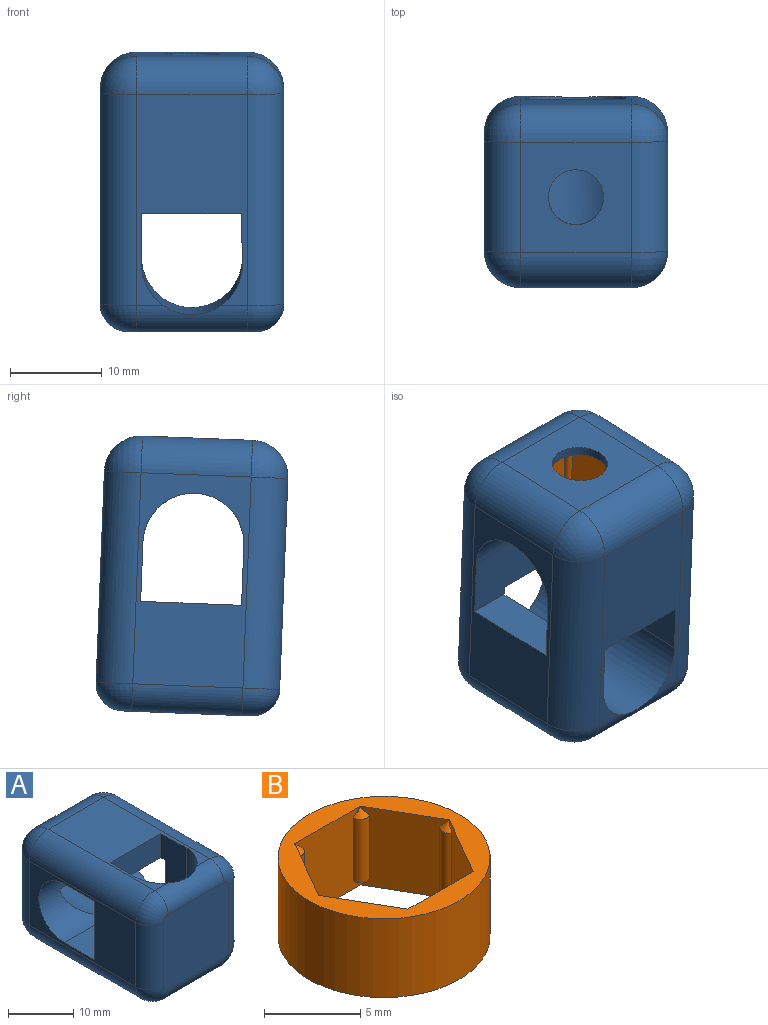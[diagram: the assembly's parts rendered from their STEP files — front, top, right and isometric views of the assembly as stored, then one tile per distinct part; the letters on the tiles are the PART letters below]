
ASSEMBLY  parts=2 mates=1
PART A: 40 faces, bbox 20x30x20 mm
  f0: cylinder r=5.5mm len=11mm, axis (-1,0,0), area 112.3mm2, adj f3,f13,f15,f18
  f1: plane 20x5.5mm, normal (1,0,0), area 99mm2, adj f2,f6,f7,f10,f11,f13,f15,f16
  f2: plane 10.87x4.5mm, normal (0,-1,0), area 48.9mm2, adj f1,f5,f10,f13
  f3: plane 23x12mm, normal (1,0,0), area 157mm2, adj f0,f12,f13,f15,f25,f28,f31,f32
  f4: plane 23x12mm, normal (-1,0,0), area 157mm2, adj f13,f14,f15,f16,f20,f21,f22,f39
  f5: plane 20x5.36mm, normal (-1,-0.02,0), area 96.3mm2, adj f2,f6,f7,f10,f11,f12,f13,f15
  f6: cylinder r=5.5mm len=20mm, axis (0,0,-1), area 347.1mm2, adj f1,f5,f10,f11,f35,f36
  f7: plane 10.87x4.5mm, normal (0,-1,0), area 48.9mm2, adj f1,f5,f11,f15
  f8: plane 12x12mm, normal (0,1,0), area 115.7mm2, adj f17,f21,f26,f27,f31
  f9: plane 14x14mm, normal (0,-1,0), area 195.1mm2, adj f32,f33,f34,f35,f36,f37,f38,f39
  f10: plane 23x12mm, normal (0,0,1), area 172.6mm2, adj f1,f2,f5,f6,f20,f25,f26,f35
  f11: plane 23x12mm, normal (0,0,-1), area 172.6mm2, adj f1,f5,f6,f7,f22,f27,f28,f36
  f12: plane 11x4.61mm, normal (0,1,0), area 50.7mm2, adj f3,f5,f13,f15
  f13: plane 20x6.5mm, normal (0,0,-1), area 119.1mm2, adj f0,f1,f2,f3,f4,f5,f12,f14
  f14: cylinder r=5.5mm len=11mm, axis (-1,0,0), area 112.3mm2, adj f4,f13,f15,f18
  f15: plane 20x6.5mm, normal (0,0,1), area 119.1mm2, adj f0,f1,f3,f4,f5,f7,f12,f14
  f16: plane 11x4.5mm, normal (0,1,0), area 49.5mm2, adj f1,f4,f13,f15
  f17: cylinder r=3mm len=6mm, axis (0,1,0), area 18.8mm2, adj f8,f19
  f18: cylinder r=5.5mm len=11mm, axis (0,1,0), area 241.9mm2, adj f0,f14,f19
  f19: plane 11x11mm, normal (0,-1,0), area 66.8mm2, adj f17,f18
  f20: cylinder r=4mm len=23mm, axis (0,1,0), area 144.5mm2, adj f4,f10,f23,f37
  f21: cylinder r=4mm len=12mm, axis (0,0,-1), area 75.4mm2, adj f4,f8,f23,f24
  f22: cylinder r=4mm len=23mm, axis (0,-1,0), area 144.5mm2, adj f4,f11,f24,f38
  f23: sphere r=4mm, area 25.1mm2, adj f20,f21,f26
  f24: sphere r=4mm, area 25.1mm2, adj f21,f22,f27
  f25: cylinder r=4mm len=23mm, axis (0,-1,0), area 144.5mm2, adj f3,f10,f29,f33
  f26: cylinder r=4mm len=12mm, axis (1,0,0), area 75.4mm2, adj f8,f10,f23,f29
  f27: cylinder r=4mm len=12mm, axis (-1,0,0), area 75.4mm2, adj f8,f11,f24,f30
  f28: cylinder r=4mm len=23mm, axis (0,1,0), area 144.5mm2, adj f3,f11,f30,f34
  f29: sphere r=4mm, area 25.1mm2, adj f25,f26,f31
  f30: sphere r=4mm, area 25.1mm2, adj f27,f28,f31
  f31: cylinder r=4mm len=12mm, axis (0,0,1), area 75.4mm2, adj f3,f8,f29,f30
  f32: cylinder r=3mm len=12mm, axis (0,0,-1), area 56.5mm2, adj f3,f9,f33,f34
  f33: torus R=1mm, axis (0,-1,0), area 21.5mm2, adj f9,f25,f32,f35
  f34: torus R=1mm, axis (0,-1,0), area 21.5mm2, adj f9,f28,f32,f36
  f35: cylinder r=3mm len=12mm, axis (-1,0,0), area 52.2mm2, adj f6,f9,f10,f33,f37
  f36: cylinder r=3mm len=12mm, axis (1,0,0), area 52.2mm2, adj f6,f9,f11,f34,f38
  f37: torus R=1mm, axis (0,-1,0), area 21.5mm2, adj f9,f20,f35,f39
  f38: torus R=1mm, axis (0,-1,0), area 21.5mm2, adj f9,f22,f36,f39
  f39: cylinder r=3mm len=12mm, axis (0,0,1), area 56.5mm2, adj f4,f9,f37,f38
PART B: 27 faces, bbox 11x11x5 mm
  f0: plane 5x4.15mm, normal (0.87,-0.5,0), area 19.5mm2, adj f7,f8,f21,f22,f23,f24,f25,f26
  f1: plane 5x4.79mm, normal (0,-1,0), area 19.5mm2, adj f7,f8,f9,f10,f11,f21,f22,f23
  f2: plane 5x4.15mm, normal (-0.87,-0.5,0), area 19.5mm2, adj f7,f8,f9,f10,f11,f15,f16,f17
  f3: plane 5x4.15mm, normal (-0.87,0.5,0), area 19.5mm2, adj f7,f8,f12,f13,f14,f15,f16,f17
  f4: plane 5x4.79mm, normal (0,1,0), area 19.5mm2, adj f7,f8,f12,f13,f14,f18,f19,f20
  f5: plane 5x4.15mm, normal (0.87,0.5,0), area 19.5mm2, adj f7,f8,f18,f19,f20,f24,f25,f26
  f6: cylinder r=5.5mm len=11mm, axis (0,0,-1), area 172.8mm2, adj f7,f8
  f7: plane 11x11mm, normal (0,0,1), area 35.4mm2, adj f0,f1,f2,f3,f4,f5,f6
  f8: plane 11x11mm, normal (0,0,-1), area 35.4mm2, adj f0,f1,f2,f3,f4,f5,f6
  f9: cylinder r=0.5mm len=4mm, axis (0,0,-1), area 4.2mm2, adj f1,f2,f10,f11
  f10: cone r=0.5mm half-angle=45deg, axis (0,0,-1), area 0.4mm2, adj f1,f2,f9
  f11: cone r=0.5mm half-angle=45deg, axis (0,0,1), area 0.4mm2, adj f1,f2,f9
  f12: cylinder r=0.5mm len=4mm, axis (0,0,-1), area 4.2mm2, adj f3,f4,f13,f14
  f13: cone r=0.5mm half-angle=45deg, axis (0,0,-1), area 0.4mm2, adj f3,f4,f12
  f14: cone r=0.5mm half-angle=45deg, axis (0,0,1), area 0.4mm2, adj f3,f4,f12
  f15: cylinder r=0.5mm len=4mm, axis (0,0,-1), area 4.2mm2, adj f2,f3,f16,f17
  f16: cone r=0.5mm half-angle=45deg, axis (0,0,-1), area 0.4mm2, adj f2,f3,f15
  f17: cone r=0.5mm half-angle=45deg, axis (0,0,1), area 0.4mm2, adj f2,f3,f15
  f18: cylinder r=0.5mm len=4mm, axis (0,0,-1), area 4.2mm2, adj f4,f5,f19,f20
  f19: cone r=0.5mm half-angle=45deg, axis (0,0,-1), area 0.4mm2, adj f4,f5,f18
  f20: cone r=0.5mm half-angle=45deg, axis (0,0,1), area 0.4mm2, adj f4,f5,f18
  f21: cylinder r=0.5mm len=4mm, axis (0,0,-1), area 4.2mm2, adj f0,f1,f22,f23
  f22: cone r=0.5mm half-angle=45deg, axis (0,0,-1), area 0.4mm2, adj f0,f1,f21
  f23: cone r=0.5mm half-angle=45deg, axis (0,0,1), area 0.4mm2, adj f0,f1,f21
  f24: cylinder r=0.5mm len=4mm, axis (0,0,-1), area 4.2mm2, adj f0,f5,f25,f26
  f25: cone r=0.5mm half-angle=45deg, axis (0,0,-1), area 0.4mm2, adj f0,f5,f24
  f26: cone r=0.5mm half-angle=45deg, axis (0,0,1), area 0.4mm2, adj f0,f5,f24
PLACE A rot(axis=(1,0,0),92.2deg) t=(12.85,23.43,11.22)mm
PLACE B rot(axis=(1,0,0),2.2deg) t=(12.85,13.09,19.82)mm
MATE fastened A.f17 <-> B.f6  axis (0,0.04,-1) through (12.85,12.89,24.82)mm
